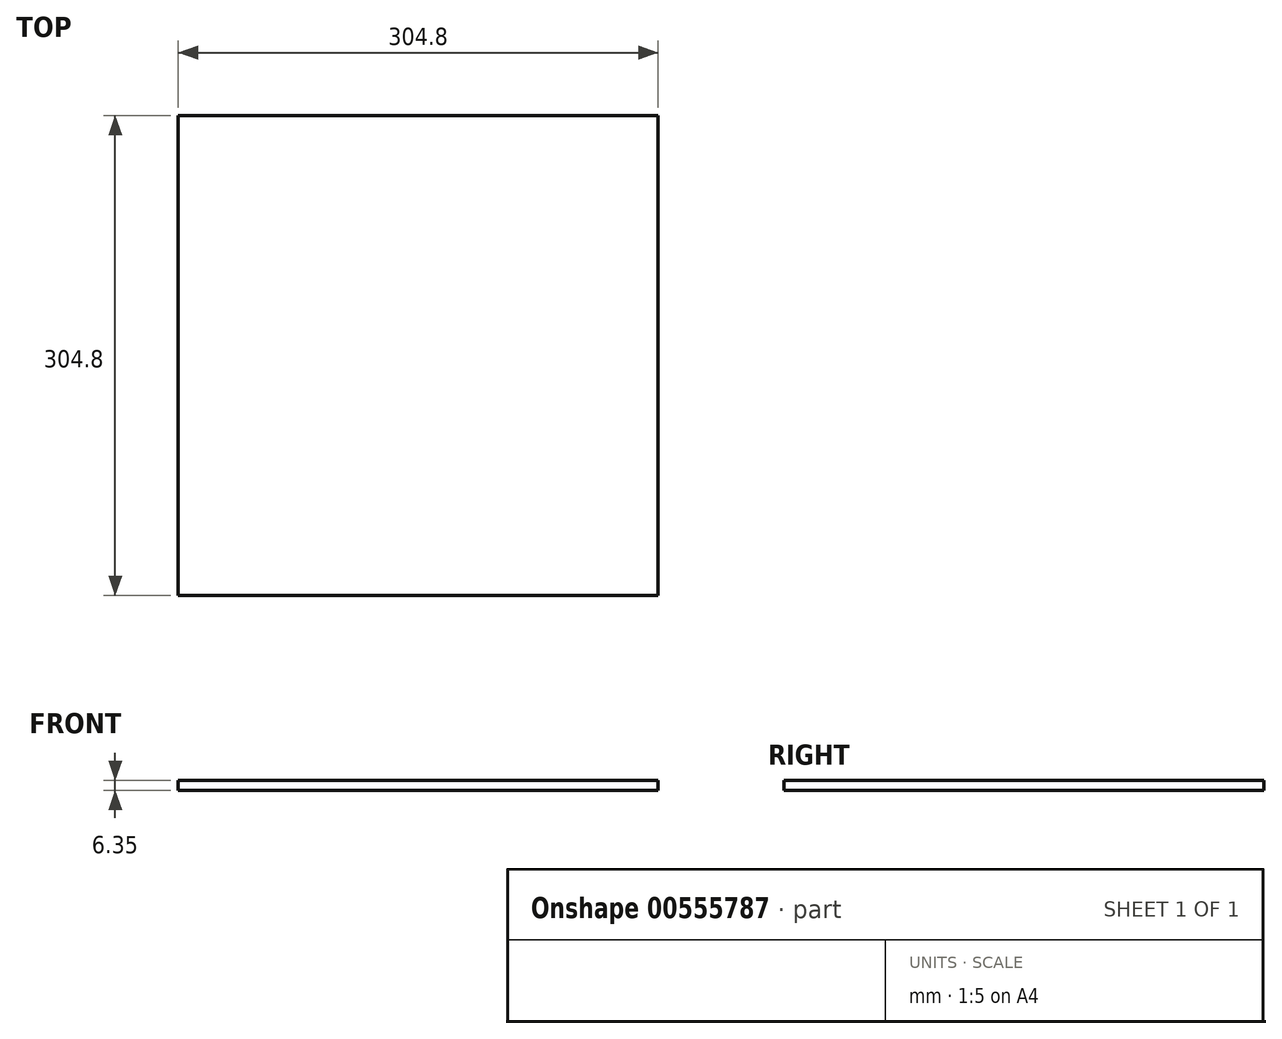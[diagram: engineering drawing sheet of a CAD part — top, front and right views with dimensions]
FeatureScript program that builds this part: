
annotation { "Feature Type Name" : "Feature", "Feature Type Description" : "" }
export const myFeature = defineFeature(function(context is Context, id is Id, definition is map)
    precondition{}
    {
        {
            var Q0;
            Q0=qCreatedBy(makeId("Top.planeOp"),FACE);
            var sketch = newSketch(context, id + "F0", { "sketchPlane" : qUnion([Q0])});
            skLineSegment(sketch, "E0.bottom", {"start": v(-152.4, -152.4) * mm, "end": v(152.4, -152.4) * mm});
            skLineSegment(sketch, "E0.top", {"start": v(-152.4, 152.4) * mm, "end": v(152.4, 152.4) * mm});
            skLineSegment(sketch, "E0.left", {"start": v(-152.4, -152.4) * mm, "end": v(-152.4, 152.4) * mm});
            skLineSegment(sketch, "E0.right", {"start": v(152.4, -152.4) * mm, "end": v(152.4, 152.4) * mm});
            skPoint(sketch, "E0.middle", {"position": v(0, 0) * mm});
            skSolve(sketch);
        }
        {
            var Q0;
            Q0 = qSketchRegion(id + "F0", true);
            extrude(context, id + "F1", {"entities" : qUnion([Q0]), "oppositeDirection" : true, "depth" : 6.35 * mm, "offsetDistance" : 25.4 * mm});
        }
    });
